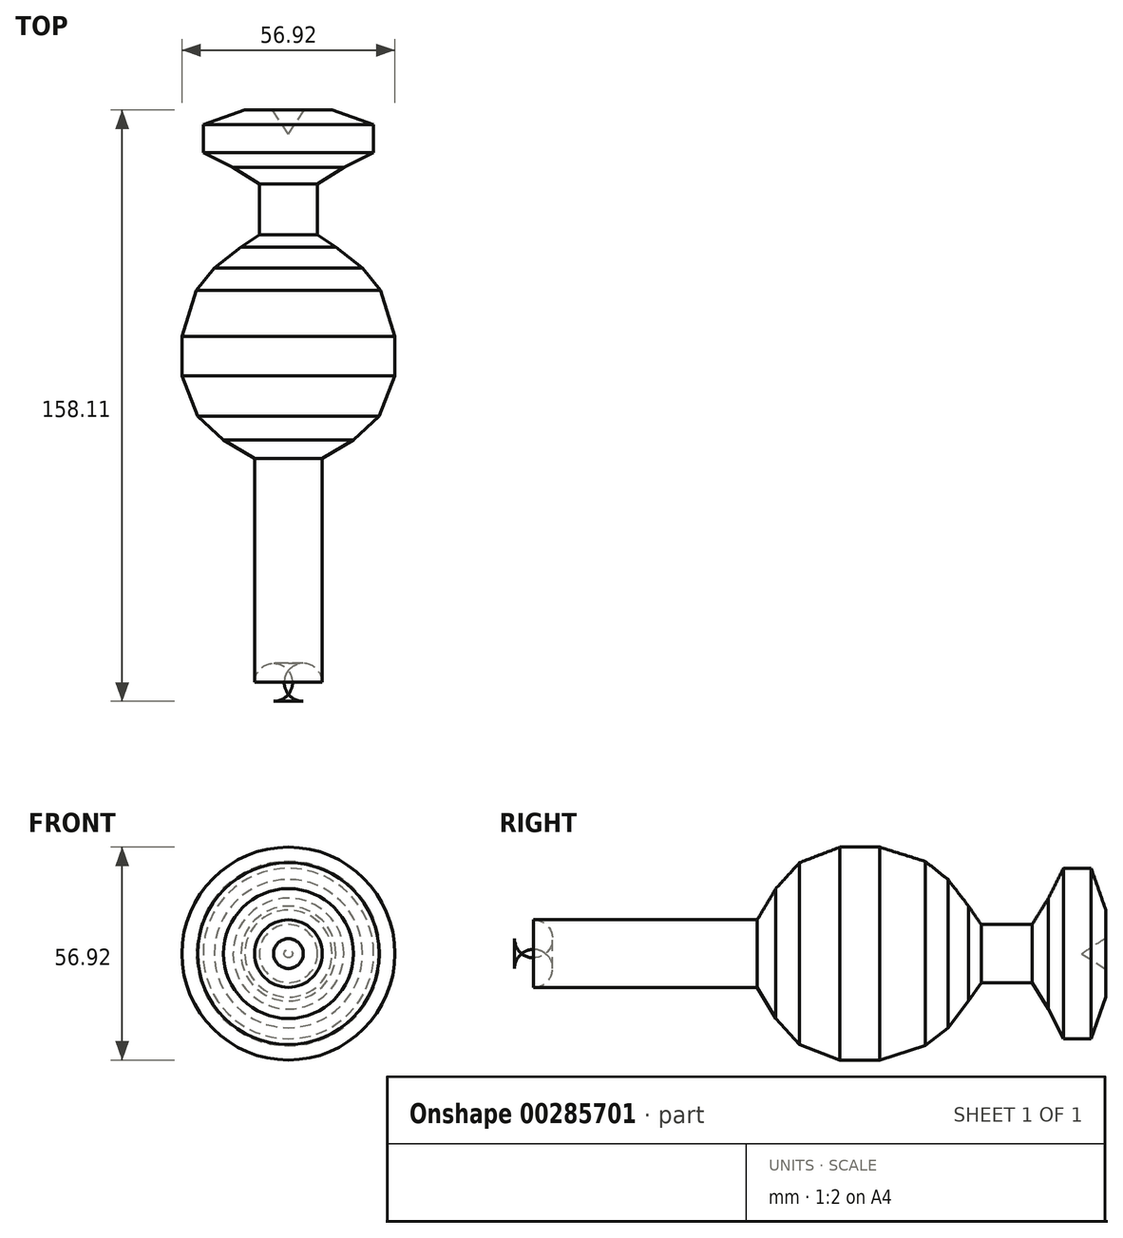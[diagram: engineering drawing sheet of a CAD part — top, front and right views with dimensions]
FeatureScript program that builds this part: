
annotation { "Feature Type Name" : "Feature", "Feature Type Description" : "" }
export const myFeature = defineFeature(function(context is Context, id is Id, definition is map)
    precondition{}
    {
        {
            var Q0;
            Q0=qCreatedBy(makeId("Right.planeOp"),FACE);
            var sketch = newSketch(context, id + "F0", { "sketchPlane" : qUnion([Q0])});
            skLineSegment(sketch, "E0", {"start": v(0, 0) * mm, "end": v(-64.9, 0) * mm});
            skLineSegment(sketch, "E1", {"start": v(-64.9, 0) * mm, "end": v(-64.9, 9.04) * mm});
            skLineSegment(sketch, "E2", {"start": v(-64.9, 9.04) * mm, "end": v(0, 9.04) * mm});
            skLineSegment(sketch, "E3", {"start": v(0, 9.04) * mm, "end": v(4.98, 17.36) * mm});
            skLineSegment(sketch, "E4", {"start": v(4.98, 17.36) * mm, "end": v(11.29, 24.3) * mm});
            skLineSegment(sketch, "E5", {"start": v(11.29, 24.3) * mm, "end": v(22.14, 28.46) * mm});
            skLineSegment(sketch, "E6", {"start": v(22.14, 28.46) * mm, "end": v(32.73, 28.46) * mm});
            skLineSegment(sketch, "E7", {"start": v(32.73, 28.46) * mm, "end": v(44.97, 24.63) * mm});
            skLineSegment(sketch, "E8", {"start": v(44.97, 24.63) * mm, "end": v(51, 19.83) * mm});
            skLineSegment(sketch, "E9", {"start": v(51, 19.83) * mm, "end": v(56.52, 12.67) * mm});
            skLineSegment(sketch, "E10", {"start": v(56.52, 12.67) * mm, "end": v(59.9, 7.77) * mm});
            skLineSegment(sketch, "E11", {"start": v(59.9, 7.77) * mm, "end": v(73.48, 7.77) * mm});
            skLineSegment(sketch, "E12", {"start": v(73.48, 7.77) * mm, "end": v(77.88, 14.82) * mm});
            skLineSegment(sketch, "E13", {"start": v(77.88, 14.82) * mm, "end": v(81.86, 22.8) * mm});
            skLineSegment(sketch, "E14", {"start": v(81.86, 22.8) * mm, "end": v(89.33, 22.8) * mm});
            skLineSegment(sketch, "E15", {"start": v(89.33, 22.8) * mm, "end": v(93.2, 11.65) * mm});
            skLineSegment(sketch, "E16", {"start": v(93.2, 11.65) * mm, "end": v(93.2, 4.2) * mm});
            skLineSegment(sketch, "E17", {"start": v(93.2, 4.2) * mm, "end": v(86.77, 0) * mm});
            skLineSegment(sketch, "E18", {"start": v(86.77, 0) * mm, "end": v(0, 0) * mm});
            skSolve(sketch);
        }
        {
            var Q0;
            Q0=makeQuery(id+"F0.imprint","IMPRINT",FACE,{"disambiguationData":[TD([[makeQuery(id+"F0.imprint","IMPRINT",EDGE,{"derivedFrom":sQuery(id+"F0.wireOp",EDGE,"E0")}),-1.0]])]});
            var Q1;
            Q1=sQuery(id+"F0.wireOp",EDGE,"E0");
            revolve(context, id + "F1", {"entities" : qUnion([Q0]), "axis" : qUnion([Q1]), "revolveType" : RevolveType.FULL});
        }
        {
            var Q0;
            Q0=makeQuery(id+"F1.opRevolve","SWEPT_EDGE",EDGE,{"disambiguationData":[OSD([sQuery(id+"F0.wireOp",EDGE,"E1"),sQuery(id+"F0.wireOp",EDGE,"E2")])]});
            fillet(context, id + "F2", {"entities" : qUnion([Q0]), "radius" : 5.08 * mm, "tangentPropagation" : true, "allowEdgeOverflow" : false});
        }
    });
